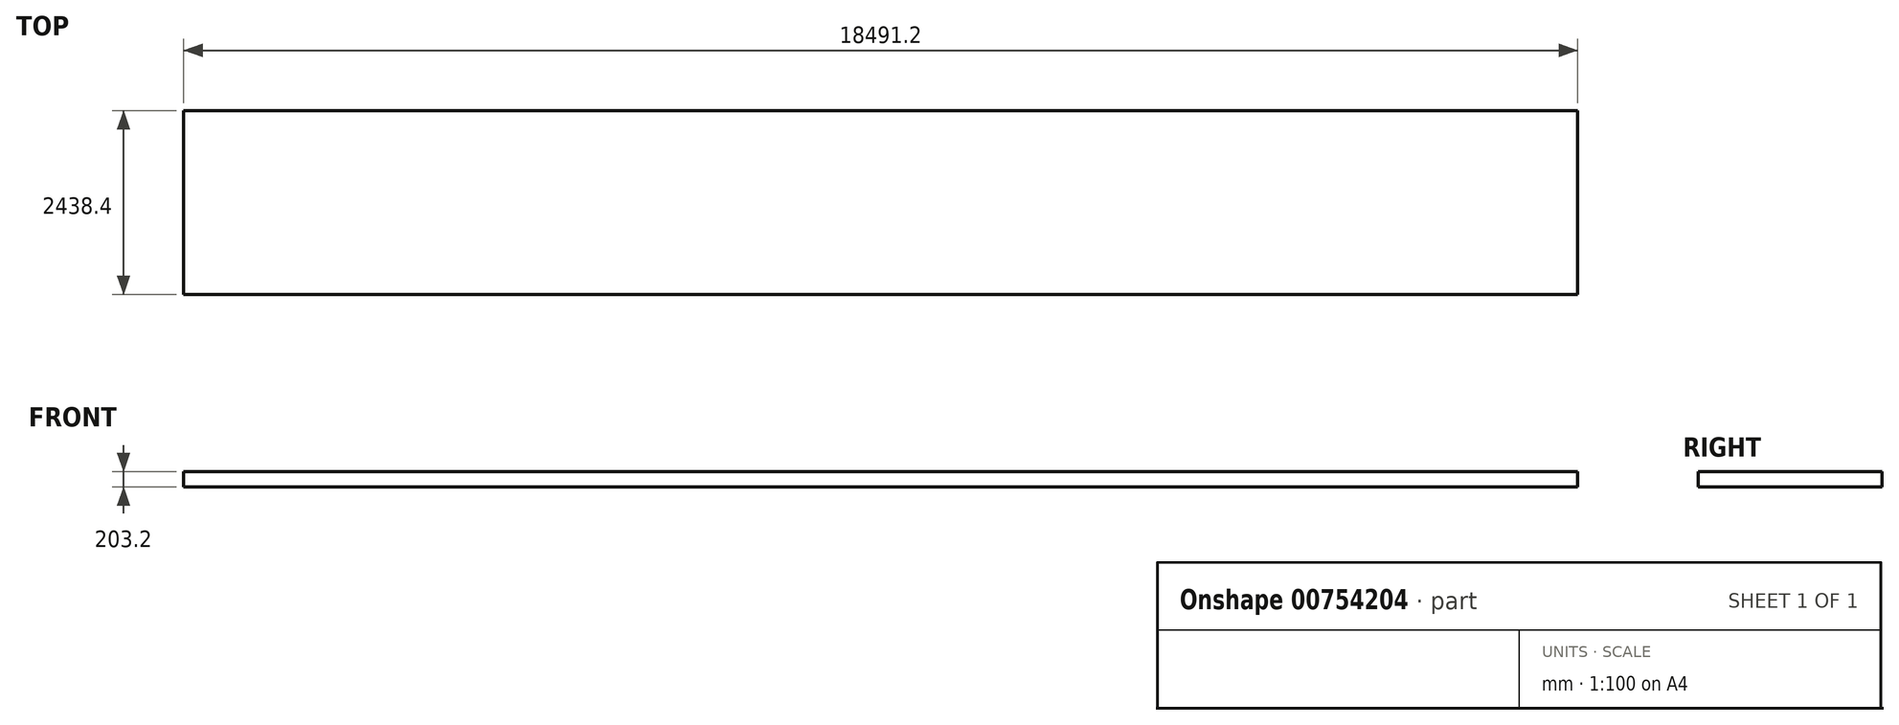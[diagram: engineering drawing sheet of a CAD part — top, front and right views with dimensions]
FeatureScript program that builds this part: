
annotation { "Feature Type Name" : "Feature", "Feature Type Description" : "" }
export const myFeature = defineFeature(function(context is Context, id is Id, definition is map)
    precondition{}
    {
        {
            var Q0;
            Q0=qCreatedBy(makeId("Top.planeOp"),FACE);
            var sketch = newSketch(context, id + "F0", { "sketchPlane" : qUnion([Q0])});
            skLineSegment(sketch, "E0.bottom", {"start": v(9245.6, 1219.2) * mm, "end": v(-9245.6, 1219.2) * mm});
            skLineSegment(sketch, "E0.top", {"start": v(9245.6, -1219.2) * mm, "end": v(-9245.6, -1219.2) * mm});
            skLineSegment(sketch, "E0.left", {"start": v(9245.6, 1219.2) * mm, "end": v(9245.6, -1219.2) * mm});
            skLineSegment(sketch, "E0.right", {"start": v(-9245.6, 1219.2) * mm, "end": v(-9245.6, -1219.2) * mm});
            skPoint(sketch, "E0.middle", {"position": v(0, 0) * mm});
            skSolve(sketch);
        }
        {
            var Q0;
            Q0=makeQuery(id+"F0.imprint","IMPRINT",FACE,{"disambiguationData":[TD([[makeQuery(id+"F0.imprint","IMPRINT",EDGE,{"derivedFrom":sQuery(id+"F0.wireOp",EDGE,"E0.bottom")}),1.0]])]});
            extrude(context, id + "F1", {"entities" : qUnion([Q0]), "depth" : 203.2 * mm, "offsetDistance" : 25.4 * mm});
        }
    });
